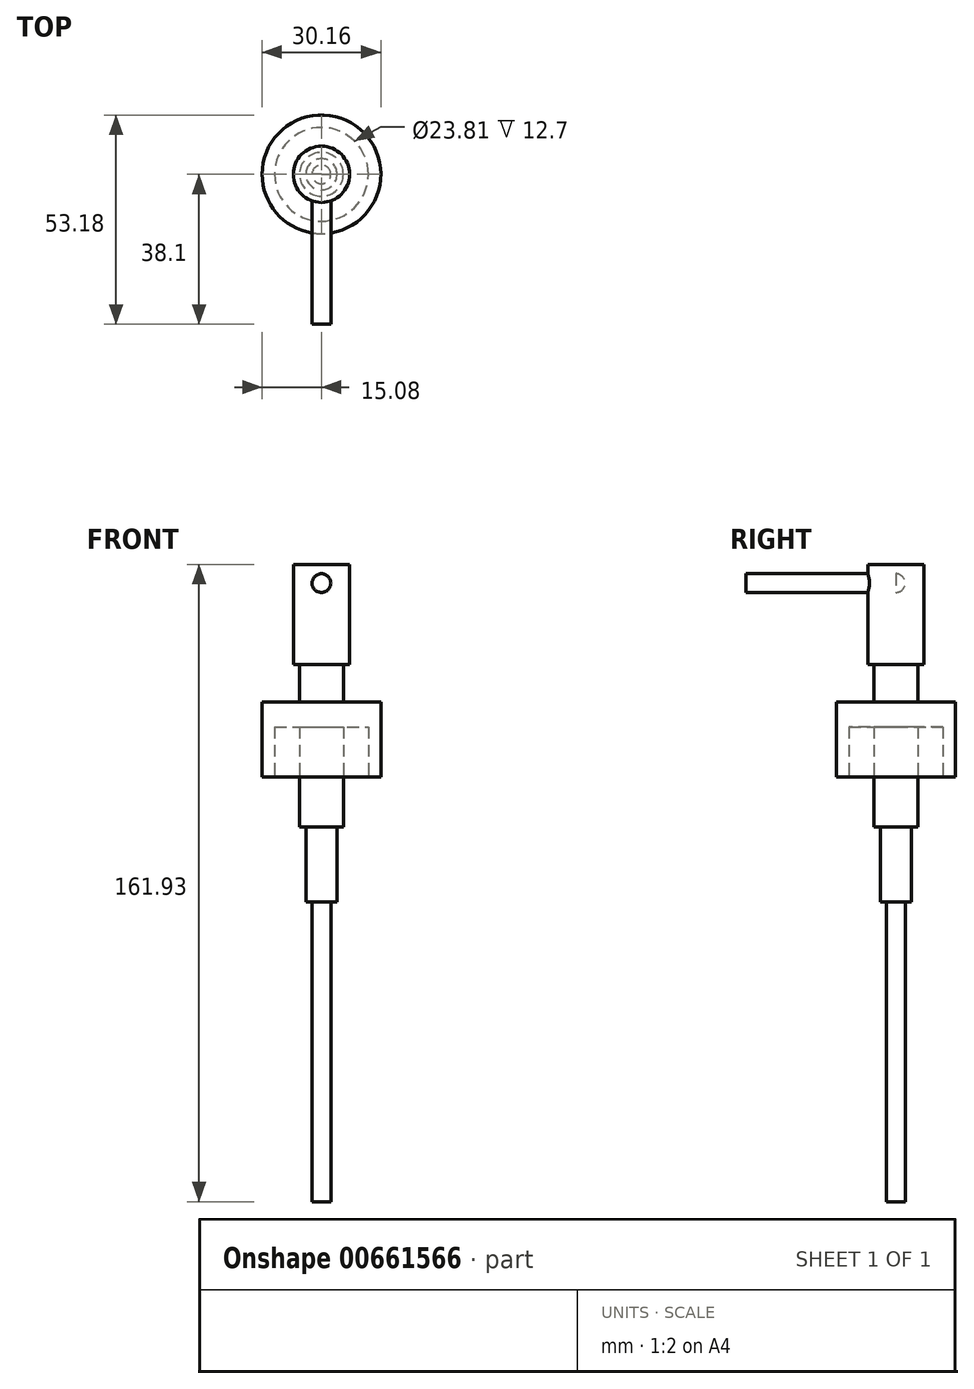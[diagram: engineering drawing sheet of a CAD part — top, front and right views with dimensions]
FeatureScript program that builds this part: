
annotation { "Feature Type Name" : "Feature", "Feature Type Description" : "" }
export const myFeature = defineFeature(function(context is Context, id is Id, definition is map)
    precondition{}
    {
        {
            var Q0;
            Q0=qCreatedBy(makeId("Front.planeOp"),FACE);
            var sketch = newSketch(context, id + "F0", { "sketchPlane" : qUnion([Q0])});
            skLineSegment(sketch, "E0", {"start": v(0, 0) * mm, "end": v(2.38, 0) * mm});
            skLineSegment(sketch, "E1", {"start": v(2.38, 0) * mm, "end": v(2.38, 76.2) * mm});
            skLineSegment(sketch, "E2", {"start": v(2.38, 76.2) * mm, "end": v(3.97, 76.2) * mm});
            skLineSegment(sketch, "E3", {"start": v(3.97, 76.2) * mm, "end": v(3.97, 95.25) * mm});
            skLineSegment(sketch, "E4", {"start": v(3.97, 95.25) * mm, "end": v(5.56, 95.25) * mm});
            skLineSegment(sketch, "E5", {"start": v(5.56, 95.25) * mm, "end": v(5.56, 120.65) * mm});
            skLineSegment(sketch, "E6", {"start": v(5.56, 120.65) * mm, "end": v(11.9, 120.65) * mm});
            skLineSegment(sketch, "E7", {"start": v(11.9, 120.65) * mm, "end": v(11.9, 107.95) * mm});
            skLineSegment(sketch, "E8", {"start": v(11.9, 107.95) * mm, "end": v(15.08, 107.95) * mm});
            skLineSegment(sketch, "E9", {"start": v(15.08, 107.95) * mm, "end": v(15.08, 127) * mm});
            skLineSegment(sketch, "E10", {"start": v(15.08, 127) * mm, "end": v(5.56, 127) * mm});
            skLineSegment(sketch, "E11", {"start": v(5.56, 127) * mm, "end": v(5.56, 136.53) * mm});
            skLineSegment(sketch, "E12", {"start": v(5.56, 136.53) * mm, "end": v(7.14, 136.53) * mm});
            skLineSegment(sketch, "E13", {"start": v(7.14, 136.53) * mm, "end": v(7.14, 161.93) * mm});
            skLineSegment(sketch, "E14", {"start": v(0, 0) * mm, "end": v(0, 161.93) * mm});
            skLineSegment(sketch, "E15", {"start": v(7.14, 161.93) * mm, "end": v(0, 161.93) * mm});
            skCircle(sketch, "E16", {"center": v(0, 157.16) * mm, "radius": 2.38 * mm});
            skSolve(sketch);
        }
        {
            var Q0;
            Q0=makeQuery(id+"F0.imprint","IMPRINT",FACE,{"disambiguationData":[TD([[makeQuery(id+"F0.imprint","IMPRINT",EDGE,{"derivedFrom":sQuery(id+"F0.wireOp",EDGE,"E0")}),1.0]])]});
            var Q1;
            Q1=sQuery(id+"F0.wireOp",EDGE,"E14");
            revolve(context, id + "F1", {"entities" : qUnion([Q0]), "axis" : qUnion([Q1]), "revolveType" : RevolveType.FULL});
        }
        {
            var Q0;
            {var subQ0=sQuery(id+"F0.wireOp",EDGE,"E16");var subQ1=sQuery(id+"F0.wireOp",EDGE,"E14");var subQ2=makeQuery(id+"F0.imprint","INTERSECT",VERTEX,{"disambiguationData":[OD(0.0)],"derivedFrom":[subQ1,subQ0]});Q0=makeQuery(id+"F0.imprint","IMPRINT",FACE,{"disambiguationData":[TD([[makeQuery(id+"F0.imprint","IMPRINT",EDGE,{"disambiguationData":[TD([[subQ2,-1.0]])],"derivedFrom":subQ1}),1.0]])]});}
            var Q1;
            {var subQ0=sQuery(id+"F0.wireOp",EDGE,"E16");var subQ1=sQuery(id+"F0.wireOp",EDGE,"E14");var subQ2=makeQuery(id+"F0.imprint","INTERSECT",VERTEX,{"disambiguationData":[OD(0.0)],"derivedFrom":[subQ1,subQ0]});Q1=makeQuery(id+"F0.imprint","IMPRINT",FACE,{"disambiguationData":[TD([[makeQuery(id+"F0.imprint","IMPRINT",EDGE,{"disambiguationData":[TD([[subQ2,-1.0]])],"derivedFrom":subQ1}),-1.0]])]});}
            extrude(context, id + "F2", {"entities" : qUnion([Q0, Q1]), "operationType" : NewBodyOperationType.ADD, "depth" : 38.1 * mm, "offsetDistance" : 25.4 * mm});
        }
    });
